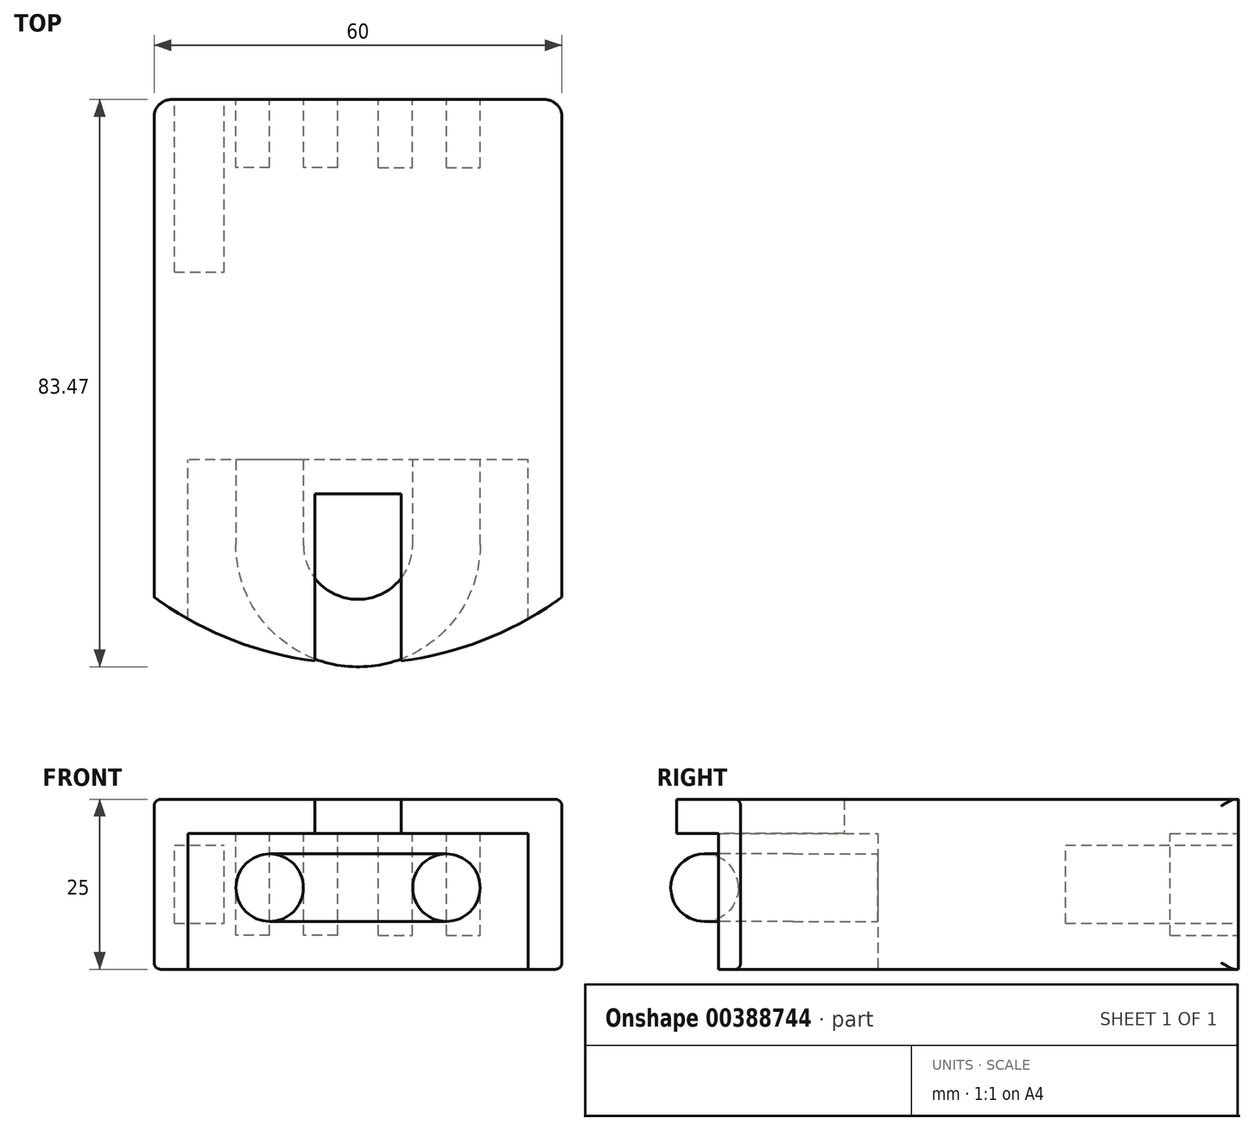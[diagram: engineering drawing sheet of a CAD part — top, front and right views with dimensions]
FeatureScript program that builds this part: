
annotation { "Feature Type Name" : "Feature", "Feature Type Description" : "" }
export const myFeature = defineFeature(function(context is Context, id is Id, definition is map)
    precondition{}
    {
        {
            var Q0;
            Q0=qCreatedBy(makeId("Top.planeOp"),FACE);
            var sketch = newSketch(context, id + "F0", { "sketchPlane" : qUnion([Q0])});
            skLineSegment(sketch, "E0.top", {"start": v(30, 36.6) * mm, "end": v(-30, 36.6) * mm});
            skLineSegment(sketch, "E0.left", {"start": v(30, -36.6) * mm, "end": v(30, 36.6) * mm});
            skLineSegment(sketch, "E0.right", {"start": v(-30, -36.6) * mm, "end": v(-30, 36.6) * mm});
            skPoint(sketch, "E0.middle", {"position": v(0, 0) * mm});
            skArc(sketch, "E1", {"start": v(-30, -36.6) * mm, "mid": v(0, -46.4) * mm, "end": v(30, -36.6) * mm});
            skSolve(sketch);
        }
        {
            var Q0;
            Q0=makeQuery(id+"F0.imprint","IMPRINT",FACE,{"disambiguationData":[TD([[makeQuery(id+"F0.imprint","IMPRINT",EDGE,{"derivedFrom":sQuery(id+"F0.wireOp",EDGE,"E0.bottom")}),-1.0]])]});
            var Q1;
            Q1=makeQuery(id+"F0.imprint","IMPRINT",FACE,{"disambiguationData":[TD([[makeQuery(id+"F0.imprint","IMPRINT",EDGE,{"derivedFrom":sQuery(id+"F0.wireOp",EDGE,"E0.top")}),1.0]])]});
            extrude(context, id + "F1", {"entities" : qUnion([Q0, Q1]), "depth" : 25 * mm});
        }
        {
            var Q0;
            Q0=qCreatedBy(makeId("Top.planeOp"),FACE);
            var sketch = newSketch(context, id + "F2", { "sketchPlane" : qUnion([Q0])});
            skLineSegment(sketch, "E2.bottom", {"start": v(-6.35, -46.4) * mm, "end": v(6.35, -46.4) * mm});
            skLineSegment(sketch, "E2.top", {"start": v(-6.35, -21.4) * mm, "end": v(6.35, -21.4) * mm});
            skLineSegment(sketch, "E2.left", {"start": v(-6.35, -46.4) * mm, "end": v(-6.35, -21.4) * mm});
            skLineSegment(sketch, "E2.right", {"start": v(6.35, -46.4) * mm, "end": v(6.35, -21.4) * mm});
            skPoint(sketch, "E2.middle", {"position": v(0, -33.9) * mm});
            skSolve(sketch);
        }
        {
            var Q0;
            Q0=makeQuery(id+"F1.opExtrude","SWEPT_EDGE",EDGE,{"disambiguationData":[OSD([sQuery(id+"F0.wireOp",EDGE,"E0.top"),sQuery(id+"F0.wireOp",EDGE,"E0.right")])]});
            var Q1;
            Q1=makeQuery(id+"F1.opExtrude","SWEPT_EDGE",EDGE,{"disambiguationData":[OSD([sQuery(id+"F0.wireOp",EDGE,"E0.top"),sQuery(id+"F0.wireOp",EDGE,"E0.left")])]});
            fillet(context, id + "F3", {"entities" : qUnion([Q0, Q1]), "radius" : 2.54 * mm, "tangentPropagation" : true, "allowEdgeOverflow" : false});
        }
        {
            var Q0;
            Q0=makeQuery(id+"F0.imprint","IMPRINT",FACE,{"disambiguationData":[TD([[makeQuery(id+"F0.imprint","IMPRINT",EDGE,{"derivedFrom":sQuery(id+"F0.wireOp",EDGE,"E0.top")}),1.0]])]});
            var sketch = newSketch(context, id + "F4", { "sketchPlane" : qUnion([Q0])});
            skLineSegment(sketch, "E3.bottom", {"start": v(25, -46.4) * mm, "end": v(-25, -46.4) * mm});
            skLineSegment(sketch, "E3.top", {"start": v(25, -16.4) * mm, "end": v(-25, -16.4) * mm});
            skLineSegment(sketch, "E3.left", {"start": v(25, -46.4) * mm, "end": v(25, -16.4) * mm});
            skLineSegment(sketch, "E3.right", {"start": v(-25, -46.4) * mm, "end": v(-25, -16.4) * mm});
            skPoint(sketch, "E3.middle", {"position": v(0, -31.4) * mm});
            skSolve(sketch);
        }
        {
            var Q0;
            Q0=qSketchRegion(id+"F4",true);
            extrude(context, id + "F5", {"entities" : qUnion([Q0]), "operationType" : NewBodyOperationType.REMOVE, "depth" : 20 * mm});
        }
        {
            var Q0;
            Q0=qSketchRegion(id+"F2",true);
            var Q1;
            Q1=makeQuery(id+"F1.opExtrude","CAP_FACE",FACE,{"disambiguationData":[OSD([sQuery(id+"F0.wireOp",EDGE,"E0.top"),sQuery(id+"F0.wireOp",EDGE,"E0.left"),sQuery(id+"F0.wireOp",EDGE,"E0.right"),sQuery(id+"F0.wireOp",EDGE,"E1")])],"isStart":false});
            extrude(context, id + "F6", {"entities" : qUnion([Q0]), "operationType" : NewBodyOperationType.REMOVE, "endBound" : BoundingType.UP_TO_SURFACE, "endBoundEntityFace" : qUnion([Q1]), "depth" : 25.4 * mm});
        }
        {
            var Q0;
            Q0=makeQuery(id+"F1.opExtrude","CAP_EDGE",EDGE,{"disambiguationData":[OSD([sQuery(id+"F0.wireOp",EDGE,"E0.left")])],"isStart":true});
            var Q1;
            Q1=makeQuery(id+"F1.opExtrude","CAP_EDGE",EDGE,{"disambiguationData":[OSD([sQuery(id+"F0.wireOp",EDGE,"E0.left")])],"isStart":false});
            var Q2;
            Q2=makeQuery(id+"F1.opExtrude","CAP_EDGE",EDGE,{"disambiguationData":[OSD([sQuery(id+"F0.wireOp",EDGE,"E0.right")])],"isStart":false});
            var Q3;
            Q3=makeQuery(id+"F1.opExtrude","CAP_EDGE",EDGE,{"disambiguationData":[OSD([sQuery(id+"F0.wireOp",EDGE,"E0.right")])],"isStart":true});
            fillet(context, id + "F7", {"entities" : qUnion([Q0, Q1, Q2, Q3]), "radius" : 1 * mm, "allowEdgeOverflow" : false});
        }
        {
            var Q0;
            Q0=makeQuery(id+"F5.boolean.opBoolean","COPY",FACE,{"derivedFrom":makeQuery(id+"F5.opExtrude","SWEPT_FACE",FACE,{"disambiguationData":[OSD([sQuery(id+"F4.wireOp",EDGE,"E3.top")])]})});
            var sketch = newSketch(context, id + "F8", { "sketchPlane" : qUnion([Q0])});
            skCircle(sketch, "E4", {"center": v(-13, 12) * mm, "radius": 5 * mm});
            skCircle(sketch, "E5.MirrorC", {"center": v(13, 12) * mm, "radius": 5 * mm});
            skSolve(sketch);
        }
        {
            var Q0;
            Q0=makeQuery(id+"F1.opExtrude","SWEPT_FACE",FACE,{"disambiguationData":[OSD([sQuery(id+"F0.wireOp",EDGE,"E0.top")])]});
            var sketch = newSketch(context, id + "F9", { "sketchPlane" : qUnion([Q0])});
            skLineSegment(sketch, "E6.bottom", {"start": v(-13, 5) * mm, "end": v(-18, 5) * mm});
            skLineSegment(sketch, "E6.top", {"start": v(-13, 20) * mm, "end": v(-18, 20) * mm});
            skLineSegment(sketch, "E6.left", {"start": v(-13, 5) * mm, "end": v(-13, 20) * mm});
            skLineSegment(sketch, "E6.right", {"start": v(-18, 5) * mm, "end": v(-18, 20) * mm});
            skPoint(sketch, "E6.middle", {"position": v(-15.5, 12.5) * mm});
            skLineSegment(sketch, "E7.MirrorCS", {"start": v(13, 5) * mm, "end": v(13, 20) * mm});
            skLineSegment(sketch, "E8.MirrorCS", {"start": v(13, 20) * mm, "end": v(18, 20) * mm});
            skLineSegment(sketch, "E9.MirrorCS", {"start": v(18, 5) * mm, "end": v(18, 20) * mm});
            skLineSegment(sketch, "E10.MirrorCS", {"start": v(13, 5) * mm, "end": v(18, 5) * mm});
            skLineSegment(sketch, "E11.bottom", {"start": v(-3, 5) * mm, "end": v(-8, 5) * mm});
            skLineSegment(sketch, "E11.top", {"start": v(-3, 20) * mm, "end": v(-8, 20) * mm});
            skLineSegment(sketch, "E11.left", {"start": v(-3, 5) * mm, "end": v(-3, 20) * mm});
            skLineSegment(sketch, "E11.right", {"start": v(-8, 5) * mm, "end": v(-8, 20) * mm});
            skPoint(sketch, "E11.middle", {"position": v(-5.5, 12.5) * mm});
            skLineSegment(sketch, "E12.MirrorCS", {"start": v(3, 20) * mm, "end": v(8, 20) * mm});
            skLineSegment(sketch, "E13.MirrorCS", {"start": v(8, 5) * mm, "end": v(8, 20) * mm});
            skLineSegment(sketch, "E14.MirrorCS", {"start": v(3, 5) * mm, "end": v(3, 20) * mm});
            skLineSegment(sketch, "E15.MirrorCS", {"start": v(3, 5) * mm, "end": v(8, 5) * mm});
            skSolve(sketch);
        }
        {
            var Q0;
            Q0=qSketchRegion(id+"F9",true);
            extrude(context, id + "F10", {"entities" : qUnion([Q0]), "operationType" : NewBodyOperationType.REMOVE, "oppositeDirection" : true, "depth" : 10 * mm});
        }
        {
            var Q0;
            Q0=makeQuery(id+"F1.opExtrude","SWEPT_FACE",FACE,{"disambiguationData":[OSD([sQuery(id+"F0.wireOp",EDGE,"E0.top")])]});
            var sketch = newSketch(context, id + "F11", { "sketchPlane" : qUnion([Q0])});
            skLineSegment(sketch, "E16.bottom", {"start": v(27, 6.75) * mm, "end": v(19.7, 6.75) * mm});
            skLineSegment(sketch, "E16.top", {"start": v(27, 18.25) * mm, "end": v(19.7, 18.25) * mm});
            skLineSegment(sketch, "E16.left", {"start": v(27, 6.75) * mm, "end": v(27, 18.25) * mm});
            skLineSegment(sketch, "E16.right", {"start": v(19.7, 6.75) * mm, "end": v(19.7, 18.25) * mm});
            skPoint(sketch, "E16.middle", {"position": v(23.35, 12.5) * mm});
            skSolve(sketch);
        }
        {
            var Q0;
            Q0=makeQuery(id+"F11.imprint","IMPRINT",FACE,{"disambiguationData":[TD([[makeQuery(id+"F11.imprint","IMPRINT",EDGE,{"derivedFrom":sQuery(id+"F11.wireOp",EDGE,"E16.bottom")}),-1.0]])]});
            extrude(context, id + "F12", {"entities" : qUnion([Q0]), "operationType" : NewBodyOperationType.REMOVE, "oppositeDirection" : true, "depth" : 25.4 * mm});
        }
        {
            var Q0;
            Q0=qCreatedBy(makeId("Top.planeOp"),FACE);
            cPlane(context, id + "F13", {"entities" : qUnion([Q0]), "cplaneType" : CPlaneType.OFFSET, "offset" : 12 * mm, "width" : 152.4 * mm, "height" : 152.4 * mm});
        }
        {
            var Q0;
            Q0=qCreatedBy(id+"F13.planeOp",FACE);
            var sketch = newSketch(context, id + "F14", { "sketchPlane" : qUnion([Q0])});
            skLineSegment(sketch, "E17", {"start": v(-13, -16.4) * mm, "end": v(-13, -28.9) * mm});
            skLineSegment(sketch, "E18", {"start": v(13, -16.4) * mm, "end": v(13, -28.9) * mm});
            skArc(sketch, "E19", {"start": v(-13, -28.9) * mm, "mid": v(0, -41.9) * mm, "end": v(13, -28.9) * mm});
            skSolve(sketch);
        }
        {
            var Q0;
            Q0=makeQuery(id+"F8.imprint","IMPRINT",FACE,{"disambiguationData":[TD([[makeQuery(id+"F8.imprint","IMPRINT",EDGE,{"derivedFrom":sQuery(id+"F8.wireOp",EDGE,"E4")}),-1.0]])]});
            var sketch = newSketch(context, id + "F15", { "sketchPlane" : qUnion([Q0])});
            skCircle(sketch, "E20", {"center": v(-13, 12) * mm, "radius": 4.97 * mm});
            skSolve(sketch);
        }
        {
            var Q0;
            Q0 = qSketchRegion(id + "F15", true);
            var Q1;
            Q1=sQuery(id+"F14.wireOp",EDGE,"E17");
            var Q2;
            Q2=sQuery(id+"F14.wireOp",EDGE,"E19");
            var Q3;
            Q3=sQuery(id+"F14.wireOp",EDGE,"E18");
            sweep(context, id + "F16", {"operationType" : NewBodyOperationType.ADD, "profiles" : qUnion([Q0]), "path" : qUnion([Q1, Q2, Q3])});
        }
    });
